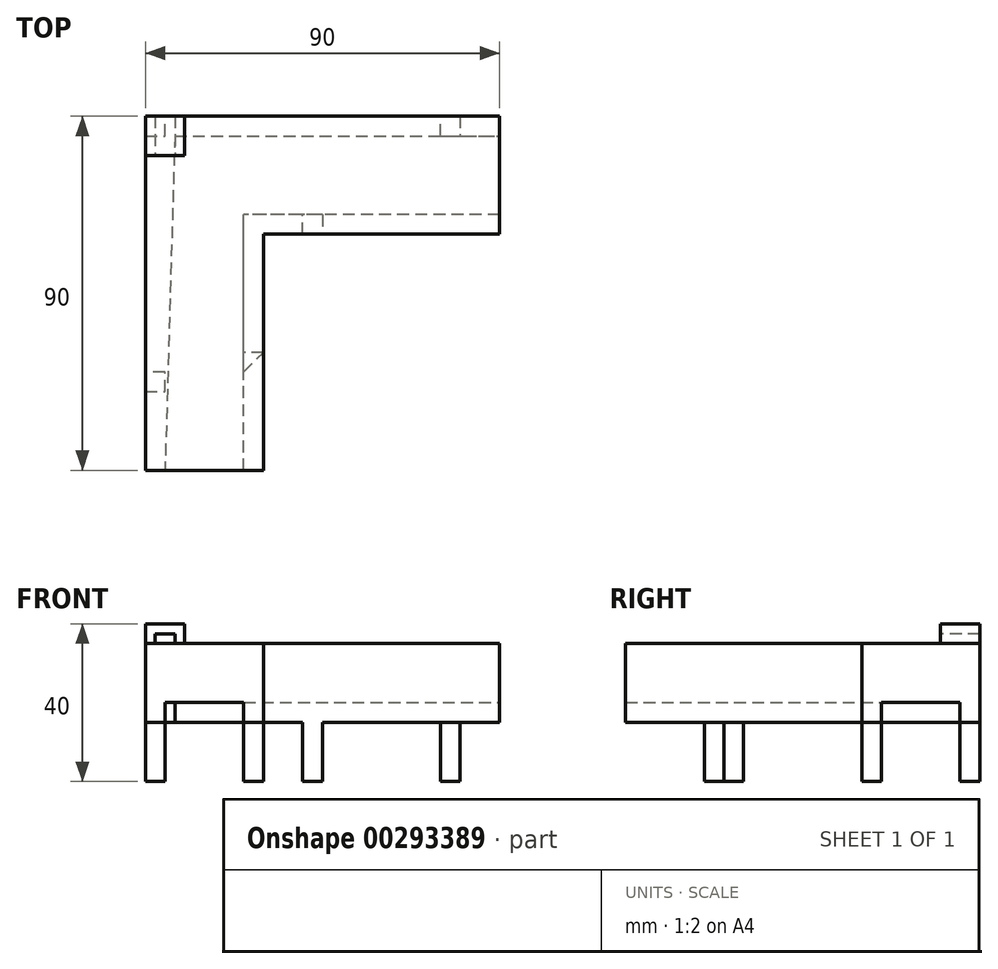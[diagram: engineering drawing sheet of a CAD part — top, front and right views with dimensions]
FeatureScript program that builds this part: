
annotation { "Feature Type Name" : "Feature", "Feature Type Description" : "" }
export const myFeature = defineFeature(function(context is Context, id is Id, definition is map)
    precondition{}
    {
        {
            var Q0;
            Q0=qCreatedBy(makeId("Top.planeOp"),FACE);
            var sketch = newSketch(context, id + "F0", { "sketchPlane" : qUnion([Q0])});
            skLineSegment(sketch, "E0.bottom", {"start": v(45, 45) * mm, "end": v(-45, 45) * mm});
            skLineSegment(sketch, "E0.top", {"start": v(45, -45) * mm, "end": v(-45, -45) * mm});
            skLineSegment(sketch, "E0.left", {"start": v(45, 45) * mm, "end": v(45, -45) * mm});
            skLineSegment(sketch, "E0.right", {"start": v(-45, 45) * mm, "end": v(-45, -45) * mm});
            skPoint(sketch, "E0.middle", {"position": v(0, 0) * mm});
            skLineSegment(sketch, "E1", {"start": v(45, 45) * mm, "end": v(45, 15) * mm});
            skLineSegment(sketch, "E2", {"start": v(-45, -45) * mm, "end": v(-15, -45) * mm});
            skLineSegment(sketch, "E3", {"start": v(-45, 45) * mm, "end": v(-45, 15) * mm});
            skLineSegment(sketch, "E4", {"start": v(-45, 45) * mm, "end": v(-15, 45) * mm});
            skLineSegment(sketch, "E5", {"start": v(-45, 15) * mm, "end": v(-15, 15) * mm});
            skLineSegment(sketch, "E6", {"start": v(-15, 15) * mm, "end": v(-15, 45) * mm});
            skLineSegment(sketch, "E7", {"start": v(-15, 15) * mm, "end": v(-15, -45) * mm});
            skLineSegment(sketch, "E8", {"start": v(-15, 15) * mm, "end": v(45, 15) * mm});
            skSolve(sketch);
        }
        {
            var Q0;
            Q0=makeQuery(id+"F0.imprint","IMPRINT",FACE,{"disambiguationData":[TD([[makeQuery(id+"F0.imprint","IMPRINT",EDGE,{"derivedFrom":sQuery(id+"F0.wireOp",EDGE,"E0.bottom")}),1.0]])]});
            var Q1;
            Q1=makeQuery(id+"F0.imprint","IMPRINT",FACE,{"disambiguationData":[TD([[makeQuery(id+"F0.imprint","IMPRINT",EDGE,{"derivedFrom":sQuery(id+"F0.wireOp",EDGE,"E3")}),1.0]])]});
            var Q2;
            Q2=makeQuery(id+"F0.imprint","IMPRINT",FACE,{"disambiguationData":[TD([[makeQuery(id+"F0.imprint","IMPRINT",EDGE,{"derivedFrom":sQuery(id+"F0.wireOp",EDGE,"E0.right")}),1.0]])]});
            extrude(context, id + "F1", {"entities" : qUnion([Q0, Q1, Q2]), "depth" : 20 * mm});
        }
        {
            var Q0;
            Q0=makeQuery(id+"F1.opExtrude","CAP_FACE",FACE,{"disambiguationData":[OSD([sQuery(id+"F0.wireOp",EDGE,"E0.bottom"),sQuery(id+"F0.wireOp",EDGE,"E0.right"),sQuery(id+"F0.wireOp",EDGE,"E1"),sQuery(id+"F0.wireOp",EDGE,"E2"),sQuery(id+"F0.wireOp",EDGE,"E3"),sQuery(id+"F0.wireOp",EDGE,"E4"),sQuery(id+"F0.wireOp",EDGE,"E7"),sQuery(id+"F0.wireOp",EDGE,"E8")])],"isStart":true});
            var sketch = newSketch(context, id + "F2", { "sketchPlane" : qUnion([Q0])});
            skLineSegment(sketch, "E9", {"start": v(45, -45) * mm, "end": v(45, -40) * mm});
            skLineSegment(sketch, "E10", {"start": v(45, -15) * mm, "end": v(45, -20) * mm});
            skLineSegment(sketch, "E11", {"start": v(-15, -15) * mm, "end": v(-15, -20) * mm});
            skLineSegment(sketch, "E12", {"start": v(-13.22, -45) * mm, "end": v(-13.22, -40) * mm});
            skLineSegment(sketch, "E13", {"start": v(-15, 45) * mm, "end": v(-20, 45) * mm});
            skLineSegment(sketch, "E14", {"start": v(-45, 45) * mm, "end": v(-40, 45) * mm});
            skLineSegment(sketch, "E15", {"start": v(-45, 6.52) * mm, "end": v(-40, 6.52) * mm});
            skLineSegment(sketch, "E16", {"start": v(-15, 3) * mm, "end": v(-20, 3) * mm});
            skLineSegment(sketch, "E17", {"start": v(-45, -45) * mm, "end": v(-45, -37.5) * mm});
            skLineSegment(sketch, "E18", {"start": v(-45, -12.52) * mm, "end": v(-40, -12.52) * mm});
            skLineSegment(sketch, "E19", {"start": v(-45, -45) * mm, "end": v(-37.5, -45) * mm});
            skLineSegment(sketch, "E20", {"start": v(-37.5, -45) * mm, "end": v(-37.5, -40) * mm});
            skLineSegment(sketch, "E21", {"start": v(-37.5, -40) * mm, "end": v(45, -40) * mm});
            skLineSegment(sketch, "E22", {"start": v(-37.5, -40) * mm, "end": v(-40, 45) * mm});
            skLineSegment(sketch, "E23", {"start": v(-15, -15) * mm, "end": v(-20, -15) * mm});
            skLineSegment(sketch, "E24", {"start": v(-20, -15) * mm, "end": v(-20, -20) * mm});
            skLineSegment(sketch, "E25", {"start": v(-20, -20) * mm, "end": v(-15, -20) * mm});
            skLineSegment(sketch, "E26", {"start": v(45, -20) * mm, "end": v(-20, -20) * mm});
            skLineSegment(sketch, "E27", {"start": v(-20, -20) * mm, "end": v(-20, 45) * mm});
            skSolve(sketch);
        }
        {
            var Q0;
            {var subQ10=sQuery(id+"F2.wireOp",EDGE,"E22");var subQ12=makeQuery(id+"F2.imprint","INTERSECT",VERTEX,{"derivedFrom":[sQuery(id+"F2.wireOp",EDGE,"E15"),subQ10]});Q0=makeQuery(id+"F2.imprint","IMPRINT",FACE,{"disambiguationData":[TD([[makeQuery(id+"F2.imprint","IMPRINT",EDGE,{"disambiguationData":[TD([[subQ12,1.0]])],"derivedFrom":subQ10}),-1.0]])]});}
            extrude(context, id + "F3", {"entities" : qUnion([Q0]), "operationType" : NewBodyOperationType.REMOVE, "oppositeDirection" : true, "depth" : 5 * mm});
        }
        {
            var Q0;
            {var subQ0=sQuery(id+"F0.wireOp",EDGE,"E2");var subQ1=sQuery(id+"F0.wireOp",EDGE,"E1");var subQ2=sQuery(id+"F0.wireOp",EDGE,"E3");var subQ3=sQuery(id+"F0.wireOp",EDGE,"E0.right");var subQ4=sQuery(id+"F0.wireOp",EDGE,"E4");var subQ5=sQuery(id+"F0.wireOp",EDGE,"E0.bottom");Q0=makeQuery(id+"F3.boolean.opBoolean","SPLIT",FACE,{"disambiguationData":[TD([makeQuery(id+"F3.opExtrude","SWEPT_FACE",FACE,{"disambiguationData":[OSD([sQuery(id+"F2.wireOp",EDGE,"E21")])]})])],"derivedFrom":makeQuery(id+"F1.opExtrude","CAP_FACE",FACE,{"disambiguationData":[OSD([subQ5,subQ3,subQ1,subQ0,subQ2,subQ4,sQuery(id+"F0.wireOp",EDGE,"E7"),sQuery(id+"F0.wireOp",EDGE,"E8")])],"isStart":true})});}
            var sketch = newSketch(context, id + "F4", { "sketchPlane" : qUnion([Q0])});
            skLineSegment(sketch, "E28", {"start": v(45, -45) * mm, "end": v(35, -45) * mm});
            skLineSegment(sketch, "E29", {"start": v(35, -45) * mm, "end": v(35, -40) * mm});
            skLineSegment(sketch, "E30", {"start": v(35, -40) * mm, "end": v(30, -40) * mm});
            skLineSegment(sketch, "E31", {"start": v(30, -40) * mm, "end": v(30, -45) * mm});
            skLineSegment(sketch, "E32", {"start": v(30, -45) * mm, "end": v(35, -45) * mm});
            skLineSegment(sketch, "E33", {"start": v(-25, -45) * mm, "end": v(-30, -45) * mm});
            skLineSegment(sketch, "E34", {"start": v(-45, -45) * mm, "end": v(-45, -40) * mm});
            skLineSegment(sketch, "E35", {"start": v(-45, -40) * mm, "end": v(-40, -40) * mm});
            skLineSegment(sketch, "E36", {"start": v(-40, -40) * mm, "end": v(-40, -45) * mm});
            skLineSegment(sketch, "E37", {"start": v(-40, -45) * mm, "end": v(-45, -45) * mm});
            skSolve(sketch);
        }
        {
            var Q0;
            Q0=makeQuery(id+"F4.imprint","IMPRINT",FACE,{"disambiguationData":[TD([[makeQuery(id+"F4.imprint","IMPRINT",EDGE,{"derivedFrom":sQuery(id+"F4.wireOp",EDGE,"E29")}),1.0]])]});
            var Q1;
            Q1=makeQuery(id+"F4.imprint","IMPRINT",FACE,{"disambiguationData":[TD([[makeQuery(id+"F4.imprint","IMPRINT",EDGE,{"derivedFrom":sQuery(id+"F4.wireOp",EDGE,"lkvs6cny-iRON-8KzY-vh8I-1erH1zl5s0BA")}),-1.0]])]});
            extrude(context, id + "F5", {"entities" : qUnion([Q0, Q1]), "operationType" : NewBodyOperationType.ADD, "depth" : 15 * mm});
        }
        {
            var Q0;
            {var subQ0=sQuery(id+"F0.wireOp",EDGE,"E8");var subQ1=sQuery(id+"F0.wireOp",EDGE,"E7");var subQ2=sQuery(id+"F0.wireOp",EDGE,"E2");var subQ3=sQuery(id+"F0.wireOp",EDGE,"E1");Q0=makeQuery(id+"F3.boolean.opBoolean","SPLIT",FACE,{"disambiguationData":[TD([makeQuery(id+"F1.opExtrude","SWEPT_FACE",FACE,{"disambiguationData":[OSD([subQ1])]})])],"derivedFrom":makeQuery(id+"F1.opExtrude","CAP_FACE",FACE,{"disambiguationData":[OSD([sQuery(id+"F0.wireOp",EDGE,"E0.bottom"),sQuery(id+"F0.wireOp",EDGE,"E0.right"),subQ3,subQ2,sQuery(id+"F0.wireOp",EDGE,"E3"),sQuery(id+"F0.wireOp",EDGE,"E4"),subQ1,subQ0])],"isStart":true})});}
            var sketch = newSketch(context, id + "F6", { "sketchPlane" : qUnion([Q0])});
            skLineSegment(sketch, "E38", {"start": v(45, -15) * mm, "end": v(35, -15) * mm});
            skLineSegment(sketch, "E39", {"start": v(25, -15) * mm, "end": v(35, -15) * mm});
            skLineSegment(sketch, "E40", {"start": v(-15, -15) * mm, "end": v(-5, -15) * mm});
            skLineSegment(sketch, "E41", {"start": v(-5, -15) * mm, "end": v(-5, -20) * mm});
            skLineSegment(sketch, "E42", {"start": v(-5, -20) * mm, "end": v(0, -20) * mm});
            skLineSegment(sketch, "E43", {"start": v(0, -20) * mm, "end": v(0, -15) * mm});
            skLineSegment(sketch, "E44", {"start": v(0, -15) * mm, "end": v(-5, -15) * mm});
            skLineSegment(sketch, "E45", {"start": v(-15, 45) * mm, "end": v(-15, 15) * mm});
            skLineSegment(sketch, "E46", {"start": v(-15, 15) * mm, "end": v(-20, 15) * mm});
            skLineSegment(sketch, "E47", {"start": v(-20, 15) * mm, "end": v(-20, 20) * mm});
            skLineSegment(sketch, "E48", {"start": v(-20, 20) * mm, "end": v(-15, 15) * mm});
            skLineSegment(sketch, "E49", {"start": v(-15, 15) * mm, "end": v(-15, 15) * mm});
            skSolve(sketch);
        }
        {
            var Q0;
            Q0=makeQuery(id+"F6.imprint","IMPRINT",FACE,{"disambiguationData":[TD([[makeQuery(id+"F6.imprint","IMPRINT",EDGE,{"derivedFrom":sQuery(id+"F6.wireOp",EDGE,"E41")}),1.0]])]});
            var Q1;
            Q1=makeQuery(id+"F6.imprint","IMPRINT",FACE,{"disambiguationData":[TD([[makeQuery(id+"F6.imprint","IMPRINT",EDGE,{"derivedFrom":sQuery(id+"F6.wireOp",EDGE,"HptapAdb-3sGT-e0cd-3NzC-WCzSCJy0pZf0")}),-1.0]])]});
            extrude(context, id + "F7", {"entities" : qUnion([Q0, Q1]), "operationType" : NewBodyOperationType.ADD, "depth" : 15 * mm});
        }
        {
            var Q0;
            Q0=makeQuery(id+"F6.imprint","IMPRINT",FACE,{"disambiguationData":[TD([[makeQuery(id+"F6.imprint","IMPRINT",EDGE,{"derivedFrom":sQuery(id+"F6.wireOp",EDGE,"E46")}),-1.0]])]});
            extrude(context, id + "F8", {"entities" : qUnion([Q0]), "operationType" : NewBodyOperationType.ADD, "depth" : 15 * mm});
        }
        {
            var Q0;
            {var subQ0=sQuery(id+"F0.wireOp",EDGE,"E2");var subQ1=sQuery(id+"F0.wireOp",EDGE,"E1");var subQ2=sQuery(id+"F0.wireOp",EDGE,"E3");var subQ3=sQuery(id+"F0.wireOp",EDGE,"E0.right");var subQ4=sQuery(id+"F0.wireOp",EDGE,"E4");var subQ5=sQuery(id+"F0.wireOp",EDGE,"E0.bottom");Q0=makeQuery(id+"F3.boolean.opBoolean","SPLIT",FACE,{"disambiguationData":[TD([makeQuery(id+"F3.opExtrude","SWEPT_FACE",FACE,{"disambiguationData":[OSD([sQuery(id+"F2.wireOp",EDGE,"E21")])]})])],"derivedFrom":makeQuery(id+"F1.opExtrude","CAP_FACE",FACE,{"disambiguationData":[OSD([subQ5,subQ3,subQ1,subQ0,subQ2,subQ4,sQuery(id+"F0.wireOp",EDGE,"E7"),sQuery(id+"F0.wireOp",EDGE,"E8")])],"isStart":true})});}
            var sketch = newSketch(context, id + "F9", { "sketchPlane" : qUnion([Q0])});
            skLineSegment(sketch, "E50", {"start": v(-45, -45) * mm, "end": v(-45, -25) * mm});
            skLineSegment(sketch, "E51", {"start": v(-45, -15) * mm, "end": v(-45, -25) * mm});
            skLineSegment(sketch, "E52", {"start": v(-45, 45) * mm, "end": v(-45, 25) * mm});
            skLineSegment(sketch, "E53", {"start": v(-45, 25) * mm, "end": v(-40, 25) * mm});
            skLineSegment(sketch, "E54", {"start": v(-40, 25) * mm, "end": v(-40, 20) * mm});
            skLineSegment(sketch, "E55", {"start": v(-40, 20) * mm, "end": v(-45, 20) * mm});
            skLineSegment(sketch, "E56", {"start": v(-45, 20) * mm, "end": v(-45, 25) * mm});
            skSolve(sketch);
        }
        {
            var Q0;
            Q0=makeQuery(id+"F9.imprint","IMPRINT",FACE,{"disambiguationData":[TD([[makeQuery(id+"F9.imprint","IMPRINT",EDGE,{"derivedFrom":sQuery(id+"F9.wireOp",EDGE,"E53")}),-1.0]])]});
            var Q1;
            Q1=makeQuery(id+"F9.imprint","IMPRINT",FACE,{"disambiguationData":[TD([[makeQuery(id+"F9.imprint","IMPRINT",EDGE,{"derivedFrom":sQuery(id+"F9.wireOp",EDGE,"Jq2nsTfA-YQ2d-kDc5-LwCm-0zst4UiHhZV3")}),1.0]])]});
            extrude(context, id + "F10", {"entities" : qUnion([Q0, Q1]), "operationType" : NewBodyOperationType.ADD, "depth" : 15 * mm});
        }
        {
            var Q0;
            Q0=makeQuery(id+"F1.opExtrude","CAP_FACE",FACE,{"disambiguationData":[OSD([sQuery(id+"F0.wireOp",EDGE,"E0.bottom"),sQuery(id+"F0.wireOp",EDGE,"E0.right"),sQuery(id+"F0.wireOp",EDGE,"E1"),sQuery(id+"F0.wireOp",EDGE,"E2"),sQuery(id+"F0.wireOp",EDGE,"E3"),sQuery(id+"F0.wireOp",EDGE,"E4"),sQuery(id+"F0.wireOp",EDGE,"E7"),sQuery(id+"F0.wireOp",EDGE,"E8")])],"isStart":false});
            var sketch = newSketch(context, id + "F11", { "sketchPlane" : qUnion([Q0])});
            skLineSegment(sketch, "E57.bottom", {"start": v(-45, 45) * mm, "end": v(-35, 45) * mm});
            skLineSegment(sketch, "E57.top", {"start": v(-45, 35) * mm, "end": v(-35, 35) * mm});
            skLineSegment(sketch, "E57.left", {"start": v(-45, 45) * mm, "end": v(-45, 35) * mm});
            skLineSegment(sketch, "E57.right", {"start": v(-35, 45) * mm, "end": v(-35, 35) * mm});
            skSolve(sketch);
        }
        {
            var Q0;
            Q0=makeQuery(id+"F11.imprint","IMPRINT",FACE,{"disambiguationData":[TD([[makeQuery(id+"F11.imprint","IMPRINT",EDGE,{"derivedFrom":sQuery(id+"F11.wireOp",EDGE,"E57.bottom")}),1.0]])]});
            extrude(context, id + "F12", {"entities" : qUnion([Q0]), "operationType" : NewBodyOperationType.ADD, "depth" : 5 * mm});
        }
        {
            var Q0;
            Q0=makeQuery(id+"F12.opExtrude","SWEPT_FACE",FACE,{"disambiguationData":[OSD([sQuery(id+"F11.wireOp",EDGE,"E57.top")])]});
            var sketch = newSketch(context, id + "F13", { "sketchPlane" : qUnion([Q0])});
            skLineSegment(sketch, "E58", {"start": v(-45, 20) * mm, "end": v(-42.5, 20) * mm});
            skLineSegment(sketch, "E59", {"start": v(-35, 20) * mm, "end": v(-37.5, 20) * mm});
            skLineSegment(sketch, "E60", {"start": v(-37.5, 20) * mm, "end": v(-37.5, 22.5) * mm});
            skLineSegment(sketch, "E61", {"start": v(-42.5, 20) * mm, "end": v(-42.5, 22.5) * mm});
            skLineSegment(sketch, "E62", {"start": v(-42.5, 22.5) * mm, "end": v(-37.5, 22.5) * mm});
            skSolve(sketch);
        }
        {
            var Q0;
            {var subQ0=sQuery(id+"F13.wireOp",EDGE,"E60");Q0=makeQuery(id+"F13.imprint","IMPRINT",FACE,{"disambiguationData":[TD([[makeQuery(id+"F13.imprint","IMPRINT",EDGE,{"derivedFrom":subQ0}),1.0]])]});}
            extrude(context, id + "F14", {"entities" : qUnion([Q0]), "operationType" : NewBodyOperationType.REMOVE, "oppositeDirection" : true, "depth" : 40 * mm});
        }
        {
            var Q0;
            Q0=makeQuery(id+"F4.imprint","IMPRINT",FACE,{"disambiguationData":[TD([[makeQuery(id+"F4.imprint","IMPRINT",EDGE,{"derivedFrom":sQuery(id+"F4.wireOp",EDGE,"E34")}),-1.0]])]});
            extrude(context, id + "F15", {"entities" : qUnion([Q0]), "operationType" : NewBodyOperationType.ADD, "depth" : 15 * mm});
        }
    });
